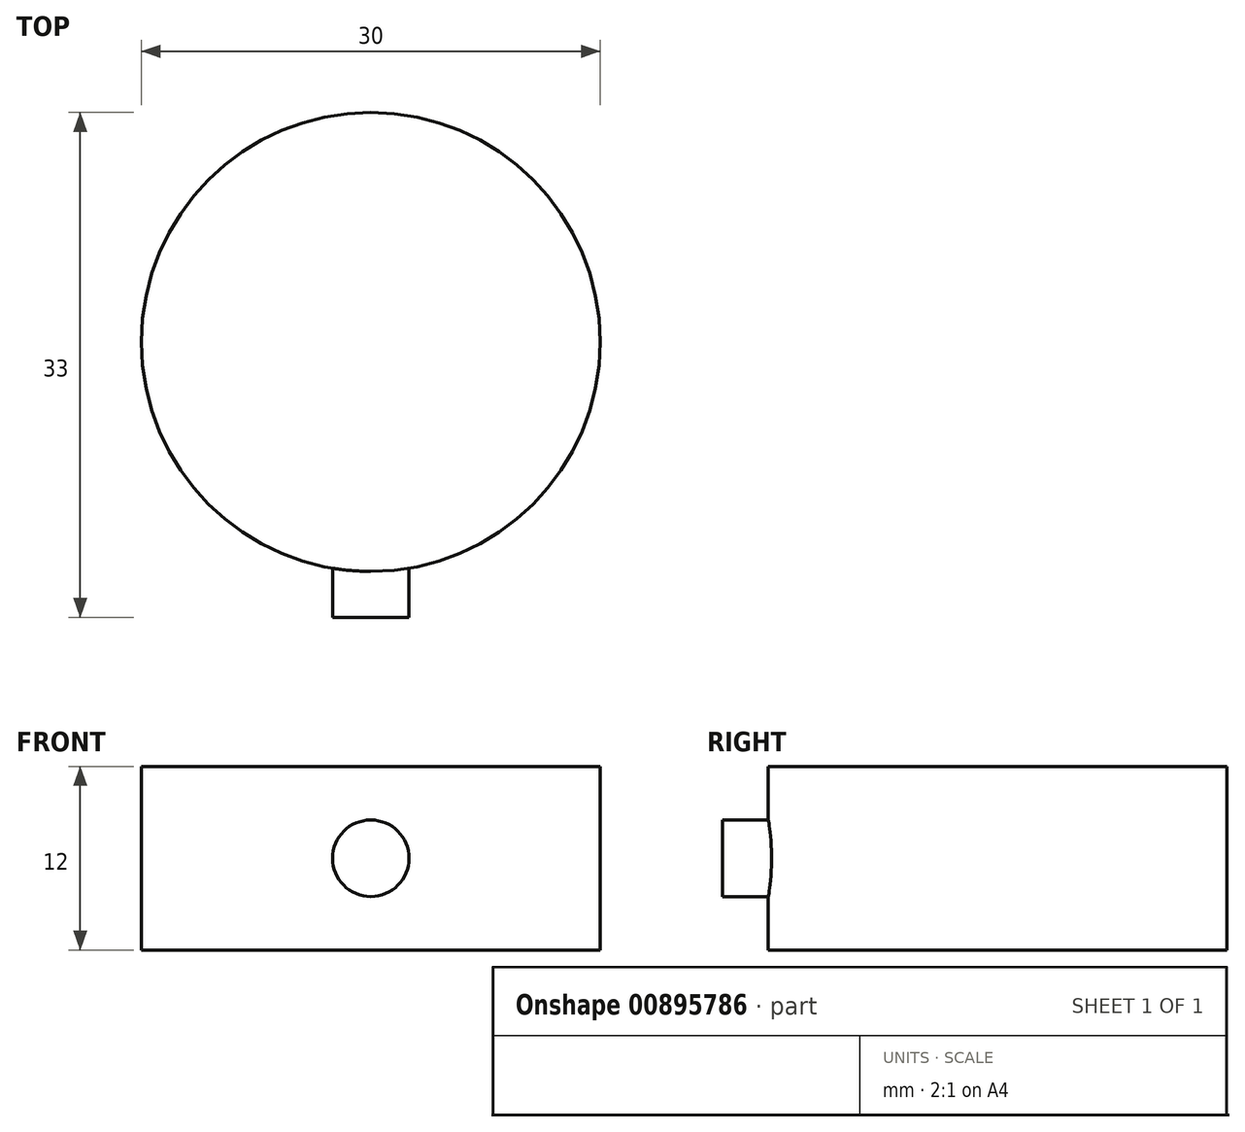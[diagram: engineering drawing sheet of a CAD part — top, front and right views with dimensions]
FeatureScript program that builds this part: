
annotation { "Feature Type Name" : "Feature", "Feature Type Description" : "" }
export const myFeature = defineFeature(function(context is Context, id is Id, definition is map)
    precondition{}
    {
        {
            var Q0;
            Q0=qCreatedBy(makeId("Top.planeOp"),FACE);
            var sketch = newSketch(context, id + "F0", { "sketchPlane" : qUnion([Q0])});
            skCircle(sketch, "E0", {"center": v(0, 0) * mm, "radius": 15 * mm});
            skSolve(sketch);
        }
        {
            var Q0;
            Q0=qSketchRegion(id+"F0",true);
            extrude(context, id + "F1", {"entities" : qUnion([Q0]), "depth" : 12 * mm, "offsetDistance" : 25 * mm});
        }
        {
            var Q0;
            Q0=qCreatedBy(makeId("Front.planeOp"),FACE);
            var sketch = newSketch(context, id + "F2", { "sketchPlane" : qUnion([Q0])});
            skCircle(sketch, "E1", {"center": v(0, 6) * mm, "radius": 2.5 * mm});
            skSolve(sketch);
        }
        {
            var Q0;
            Q0=qSketchRegion(id+"F2",true);
            extrude(context, id + "F3", {"entities" : qUnion([Q0]), "operationType" : NewBodyOperationType.ADD, "depth" : 18 * mm, "offsetDistance" : 25 * mm});
        }
    });
